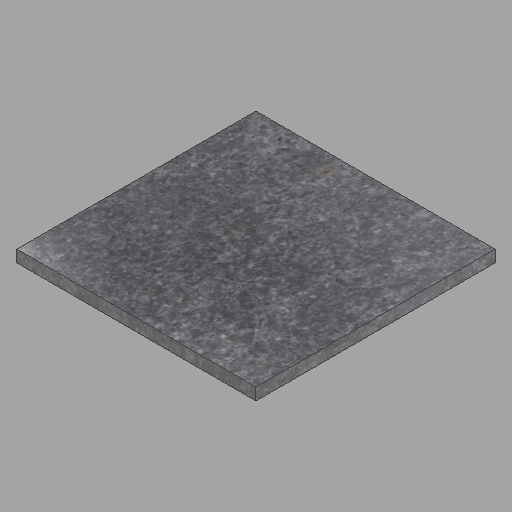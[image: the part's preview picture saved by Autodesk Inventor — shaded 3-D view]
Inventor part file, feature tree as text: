
AUTODESK INVENTOR PART (.ipt)
format: ipt  version: 2023 (Build 270158000, 158)  size: 238,080 bytes
history: native  units: in
note: dims shown in document units (in); Inventor stores cm internally (conversion verified against a paired STEP export)
features: other x1, extrude x1, sketch x1
ambient origin geometry x8: Origin, YZ Plane, XZ Plane, XY Plane, X Axis, Y Axis, Z Axis, Center Point
bodies: Solid1 (feature_tree)
feature tree (3):
  other  "1.5x30x30-14"
  extrude  "Extrusion1"  Depth=30.0in
  sketch  "Sketch1"  dims[d0=1.5in d1=30.0in d2=30.0in d3=0.0in]
